# Revit family: Faucet-Lavatory-KOHLER-Coralais-K-15182
name_source: partatom
category: Plumbing Fixtures
revit_build: Autodesk Revit 2015 (Build: 20140606_1530(x64)
units: mm (PartAtom-declared; Revit-internal decimal feet)

## types (6) — shared parameters
ADA Compliant = Yes
Assembly Code = D2010
CW Connection = Yes
Cold Water Inlet = Cold Water Inlet
Date Modified = 08/22/2018
Default Elevation = 36"
Faucet Hole Spacing = 0"
Flow Rate = 1 GPM
HW Connection = Yes
Handle Clearance = 0"
Height = 6 3/8"
Hot Water Inlet = Hot Water Inlet
Length = 4 9/16"
Manufacturer = KOHLER Co.
MasterFormat 1995 = 15410
MasterFormat 2004 = 22.41.39
Material = Premium Metal Construction
Pressure = 60.00 psi
Product Documentation Link = http://www.us.kohler.com
Product Name = Coralais
Product Page URL = http://www.us.kohler.com
Spout Reach = 4 9/16"
URL = https://www.us.kohler.com
Vent Connection = No
Waste Connection = No
Waste Water Outlet = Waste Water Outlet
Width = 6"

## per-type parameters (varying)
| type | Description | Drain Included | Finish | Model | Pop-up drain | Type |
| Plastic pop-up drain-CP-Polished Chrome | Single-handle centerset bathroom sink faucet with plastic pop-up drain and lift rod | Yes | Kohler-Metal-CP-Polished_Chrome | K-15182-4DRA-CP | Yes | 1 |
| Plastic pop-up drain-G-Brushed Chrome | Single-handle centerset bathroom sink faucet with plastic pop-up drain and lift rod | Yes | Kohler-Metal-G-Brushed_Chrome | K-15182-4DRA-G | Yes | 2 |
| Less drain-CP-Polished Chrome | Single-handle centerset bathroom sink faucet with plugged lift rod hole, less drain | No | Kohler-Metal-CP-Polished_Chrome | K-15182-4NDRA-CP | No | 3 |
| Less drain-G-Brushed Chrome | Single-handle centerset bathroom sink faucet with plugged lift rod hole, less drain | No | Kohler-Metal-G-Brushed_Chrome | K-15182-4NDRA-G | No | 4 |
| Metal pop-up drain-CP-Polished Chrome | Single-handle centerset bathroom sink faucet with metal pop-up drain and lift rod | Yes | Kohler-Metal-CP-Polished_Chrome | K-15182-4RA-CP | Yes | 5 |
| Metal pop-up drain-G-Brushed Chrome | Single-handle centerset bathroom sink faucet with metal pop-up drain and lift rod | Yes | Kohler-Metal-G-Brushed_Chrome | K-15182-4RA-G | Yes | 6 |

## geometry (parser evidence)
native form markers: Sweep x5
no freeform markers — native parametric forms only
